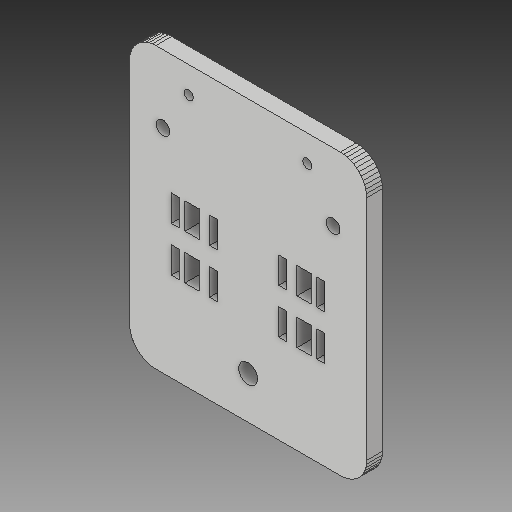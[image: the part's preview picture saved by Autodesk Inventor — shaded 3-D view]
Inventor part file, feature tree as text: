
AUTODESK INVENTOR PART (.ipt)
format: ipt  version: 2018 (Build 220112000, 112)  size: 311,296 bytes
history: native  units: mm
features: sketch x4, other x3
ambient origin geometry x8: Origin, YZ Plane, XZ Plane, XY Plane, X Axis, Y Axis, Z Axis, Center Point
bodies: Solid1 (feature_tree)
feature tree (7):
  other  "X-Axis-End-Plate.ipt"
  other  "Solid1::X-Axis-End-Plate.ipt"
  other  "TaggingFeature1"
  sketch  "Sketch1"  dims[d0=10.0mm]
  sketch  "Sketch2"
  sketch  "Sketch3"
  sketch  "Sketch4"
